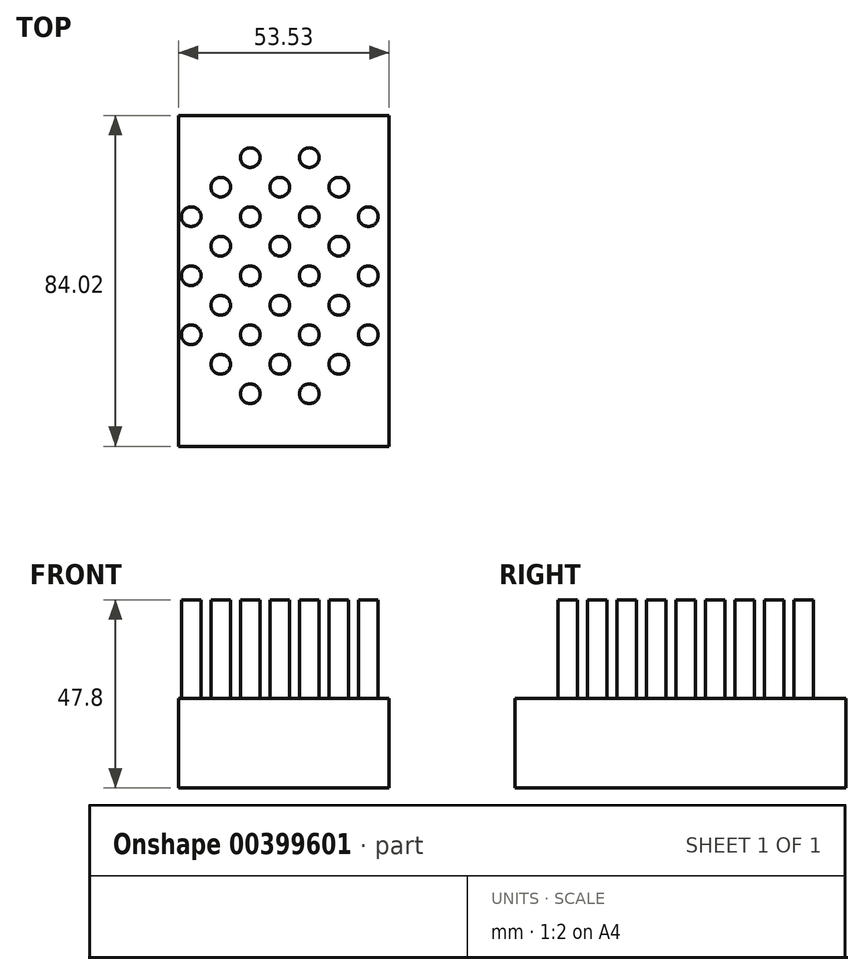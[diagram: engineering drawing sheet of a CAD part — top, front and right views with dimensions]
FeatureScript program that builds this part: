
annotation { "Feature Type Name" : "Feature", "Feature Type Description" : "" }
export const myFeature = defineFeature(function(context is Context, id is Id, definition is map)
    precondition{}
    {
        {
            var Q0;
            Q0=qCreatedBy(makeId("Top.planeOp"),FACE);
            var sketch = newSketch(context, id + "F0", { "sketchPlane" : qUnion([Q0])});
            skCircle(sketch, "E0", {"center": v(0, 8.36) * mm, "radius": 2.5 * mm});
            skCircle(sketch, "E1", {"center": v(7.5, 0.86) * mm, "radius": 2.5 * mm});
            skCircle(sketch, "E2.0.1.0", {"center": v(0, 23.36) * mm, "radius": 2.5 * mm});
            skCircle(sketch, "E2.0.1.1", {"center": v(7.5, 15.86) * mm, "radius": 2.5 * mm});
            skCircle(sketch, "E2.0.2.0", {"center": v(0, 38.36) * mm, "radius": 2.5 * mm});
            skCircle(sketch, "E2.0.2.1", {"center": v(7.5, 30.86) * mm, "radius": 2.5 * mm});
            skCircle(sketch, "E2.0.3.0", {"center": v(0, 53.36) * mm, "radius": 2.5 * mm});
            skCircle(sketch, "E2.0.3.1", {"center": v(7.5, 45.86) * mm, "radius": 2.5 * mm});
            skCircle(sketch, "E2.0.4.0", {"center": v(0, 68.36) * mm, "radius": 2.5 * mm});
            skCircle(sketch, "E2.0.4.1", {"center": v(7.5, 60.86) * mm, "radius": 2.5 * mm});
            skCircle(sketch, "E2.1.0.0", {"center": v(15, 8.36) * mm, "radius": 2.5 * mm});
            skCircle(sketch, "E2.1.0.1", {"center": v(22.5, 0.86) * mm, "radius": 2.5 * mm});
            skCircle(sketch, "E2.1.1.0", {"center": v(15, 23.36) * mm, "radius": 2.5 * mm});
            skCircle(sketch, "E2.1.1.1", {"center": v(22.5, 15.86) * mm, "radius": 2.5 * mm});
            skCircle(sketch, "E2.1.2.0", {"center": v(15, 38.36) * mm, "radius": 2.5 * mm});
            skCircle(sketch, "E2.1.2.1", {"center": v(22.5, 30.86) * mm, "radius": 2.5 * mm});
            skCircle(sketch, "E2.1.3.0", {"center": v(15, 53.36) * mm, "radius": 2.5 * mm});
            skCircle(sketch, "E2.1.3.1", {"center": v(22.5, 45.86) * mm, "radius": 2.5 * mm});
            skCircle(sketch, "E2.1.4.0", {"center": v(15, 68.36) * mm, "radius": 2.5 * mm});
            skCircle(sketch, "E2.1.4.1", {"center": v(22.5, 60.86) * mm, "radius": 2.5 * mm});
            skCircle(sketch, "E2.2.0.0", {"center": v(30, 8.36) * mm, "radius": 2.5 * mm});
            skCircle(sketch, "E2.2.0.1", {"center": v(37.5, 0.86) * mm, "radius": 2.5 * mm});
            skCircle(sketch, "E2.2.1.0", {"center": v(30, 23.36) * mm, "radius": 2.5 * mm});
            skCircle(sketch, "E2.2.1.1", {"center": v(37.5, 15.86) * mm, "radius": 2.5 * mm});
            skCircle(sketch, "E2.2.2.0", {"center": v(30, 38.36) * mm, "radius": 2.5 * mm});
            skCircle(sketch, "E2.2.2.1", {"center": v(37.5, 30.86) * mm, "radius": 2.5 * mm});
            skCircle(sketch, "E2.2.3.0", {"center": v(30, 53.36) * mm, "radius": 2.5 * mm});
            skCircle(sketch, "E2.2.3.1", {"center": v(37.5, 45.86) * mm, "radius": 2.5 * mm});
            skCircle(sketch, "E2.2.4.0", {"center": v(30, 68.36) * mm, "radius": 2.5 * mm});
            skCircle(sketch, "E2.2.4.1", {"center": v(37.5, 60.86) * mm, "radius": 2.5 * mm});
            skCircle(sketch, "E2.3.0.0", {"center": v(45, 8.36) * mm, "radius": 2.5 * mm});
            skCircle(sketch, "E2.3.0.1", {"center": v(52.5, 0.86) * mm, "radius": 2.5 * mm});
            skCircle(sketch, "E2.3.1.0", {"center": v(45, 23.36) * mm, "radius": 2.5 * mm});
            skCircle(sketch, "E2.3.1.1", {"center": v(52.5, 15.86) * mm, "radius": 2.5 * mm});
            skCircle(sketch, "E2.3.2.0", {"center": v(45, 38.36) * mm, "radius": 2.5 * mm});
            skCircle(sketch, "E2.3.2.1", {"center": v(52.5, 30.86) * mm, "radius": 2.5 * mm});
            skCircle(sketch, "E2.3.3.0", {"center": v(45, 53.36) * mm, "radius": 2.5 * mm});
            skCircle(sketch, "E2.3.3.1", {"center": v(52.5, 45.86) * mm, "radius": 2.5 * mm});
            skCircle(sketch, "E2.3.4.0", {"center": v(45, 68.36) * mm, "radius": 2.5 * mm});
            skCircle(sketch, "E2.3.4.1", {"center": v(52.5, 60.86) * mm, "radius": 2.5 * mm});
            skCircle(sketch, "E2.4.0.0", {"center": v(60, 8.36) * mm, "radius": 2.5 * mm});
            skCircle(sketch, "E2.4.0.1", {"center": v(67.5, 0.86) * mm, "radius": 2.5 * mm});
            skCircle(sketch, "E2.4.1.0", {"center": v(60, 23.36) * mm, "radius": 2.5 * mm});
            skCircle(sketch, "E2.4.1.1", {"center": v(67.5, 15.86) * mm, "radius": 2.5 * mm});
            skCircle(sketch, "E2.4.2.0", {"center": v(60, 38.36) * mm, "radius": 2.5 * mm});
            skCircle(sketch, "E2.4.2.1", {"center": v(67.5, 30.86) * mm, "radius": 2.5 * mm});
            skCircle(sketch, "E2.4.3.0", {"center": v(60, 53.36) * mm, "radius": 2.5 * mm});
            skCircle(sketch, "E2.4.3.1", {"center": v(67.5, 45.86) * mm, "radius": 2.5 * mm});
            skCircle(sketch, "E2.4.4.0", {"center": v(60, 68.36) * mm, "radius": 2.5 * mm});
            skCircle(sketch, "E2.4.4.1", {"center": v(67.5, 60.86) * mm, "radius": 2.5 * mm});
            skLineSegment(sketch, "E2.direction1", {"start": v(0, 8.36) * mm, "end": v(15, 8.36) * mm, "construction": true});
            skLineSegment(sketch, "E2.direction2", {"start": v(0, 8.36) * mm, "end": v(0, 23.36) * mm, "construction": true});
            skSolve(sketch);
        }
        {
            var Q0;
            Q0=makeQuery(id+"F0.imprint","IMPRINT",FACE,{"disambiguationData":[TD([[makeQuery(id+"F0.imprint","IMPRINT",EDGE,{"derivedFrom":sQuery(id+"F0.wireOp",EDGE,"E2.1.4.1")}),1.0]])]});
            var Q1;
            Q1=makeQuery(id+"F0.imprint","IMPRINT",FACE,{"disambiguationData":[TD([[makeQuery(id+"F0.imprint","IMPRINT",EDGE,{"derivedFrom":sQuery(id+"F0.wireOp",EDGE,"E2.2.3.0")}),1.0]])]});
            var Q2;
            Q2=makeQuery(id+"F0.imprint","IMPRINT",FACE,{"disambiguationData":[TD([[makeQuery(id+"F0.imprint","IMPRINT",EDGE,{"derivedFrom":sQuery(id+"F0.wireOp",EDGE,"E2.2.1.0")}),1.0]])]});
            var Q3;
            Q3=makeQuery(id+"F0.imprint","IMPRINT",FACE,{"disambiguationData":[TD([[makeQuery(id+"F0.imprint","IMPRINT",EDGE,{"derivedFrom":sQuery(id+"F0.wireOp",EDGE,"E2.2.0.0")}),1.0]])]});
            var Q4;
            Q4=makeQuery(id+"F0.imprint","IMPRINT",FACE,{"disambiguationData":[TD([[makeQuery(id+"F0.imprint","IMPRINT",EDGE,{"derivedFrom":sQuery(id+"F0.wireOp",EDGE,"E2.1.2.1")}),1.0]])]});
            var Q5;
            Q5=makeQuery(id+"F0.imprint","IMPRINT",FACE,{"disambiguationData":[TD([[makeQuery(id+"F0.imprint","IMPRINT",EDGE,{"derivedFrom":sQuery(id+"F0.wireOp",EDGE,"E2.2.4.1")}),1.0]])]});
            var Q6;
            Q6=makeQuery(id+"F0.imprint","IMPRINT",FACE,{"disambiguationData":[TD([[makeQuery(id+"F0.imprint","IMPRINT",EDGE,{"derivedFrom":sQuery(id+"F0.wireOp",EDGE,"E2.1.1.1")}),1.0]])]});
            var Q7;
            Q7=makeQuery(id+"F0.imprint","IMPRINT",FACE,{"disambiguationData":[TD([[makeQuery(id+"F0.imprint","IMPRINT",EDGE,{"derivedFrom":sQuery(id+"F0.wireOp",EDGE,"E2.1.0.1")}),1.0]])]});
            var Q8;
            Q8=makeQuery(id+"F0.imprint","IMPRINT",FACE,{"disambiguationData":[TD([[makeQuery(id+"F0.imprint","IMPRINT",EDGE,{"derivedFrom":sQuery(id+"F0.wireOp",EDGE,"E2.2.3.1")}),1.0]])]});
            var Q9;
            Q9=makeQuery(id+"F0.imprint","IMPRINT",FACE,{"disambiguationData":[TD([[makeQuery(id+"F0.imprint","IMPRINT",EDGE,{"derivedFrom":sQuery(id+"F0.wireOp",EDGE,"E2.2.1.1")}),1.0]])]});
            var Q10;
            Q10=makeQuery(id+"F0.imprint","IMPRINT",FACE,{"disambiguationData":[TD([[makeQuery(id+"F0.imprint","IMPRINT",EDGE,{"derivedFrom":sQuery(id+"F0.wireOp",EDGE,"E2.1.3.1")}),1.0]])]});
            var Q11;
            Q11=makeQuery(id+"F0.imprint","IMPRINT",FACE,{"disambiguationData":[TD([[makeQuery(id+"F0.imprint","IMPRINT",EDGE,{"derivedFrom":sQuery(id+"F0.wireOp",EDGE,"E2.2.2.0")}),1.0]])]});
            var Q12;
            Q12=makeQuery(id+"F0.imprint","IMPRINT",FACE,{"disambiguationData":[TD([[makeQuery(id+"F0.imprint","IMPRINT",EDGE,{"derivedFrom":sQuery(id+"F0.wireOp",EDGE,"E2.2.2.1")}),1.0]])]});
            var Q13;
            Q13=makeQuery(id+"F0.imprint","IMPRINT",FACE,{"disambiguationData":[TD([[makeQuery(id+"F0.imprint","IMPRINT",EDGE,{"derivedFrom":sQuery(id+"F0.wireOp",EDGE,"E2.3.3.0")}),1.0]])]});
            var Q14;
            Q14=makeQuery(id+"F0.imprint","IMPRINT",FACE,{"disambiguationData":[TD([[makeQuery(id+"F0.imprint","IMPRINT",EDGE,{"derivedFrom":sQuery(id+"F0.wireOp",EDGE,"E2.3.2.0")}),1.0]])]});
            var Q15;
            Q15=makeQuery(id+"F0.imprint","IMPRINT",FACE,{"disambiguationData":[TD([[makeQuery(id+"F0.imprint","IMPRINT",EDGE,{"derivedFrom":sQuery(id+"F0.wireOp",EDGE,"E2.3.1.0")}),1.0]])]});
            var Q16;
            Q16=makeQuery(id+"F0.imprint","IMPRINT",FACE,{"disambiguationData":[TD([[makeQuery(id+"F0.imprint","IMPRINT",EDGE,{"derivedFrom":sQuery(id+"F0.wireOp",EDGE,"E2.2.0.1")}),1.0]])]});
            var Q17;
            Q17=makeQuery(id+"F0.imprint","IMPRINT",FACE,{"disambiguationData":[TD([[makeQuery(id+"F0.imprint","IMPRINT",EDGE,{"derivedFrom":sQuery(id+"F0.wireOp",EDGE,"E2.3.0.0")}),1.0]])]});
            var Q18;
            Q18=makeQuery(id+"F0.imprint","IMPRINT",FACE,{"disambiguationData":[TD([[makeQuery(id+"F0.imprint","IMPRINT",EDGE,{"derivedFrom":sQuery(id+"F0.wireOp",EDGE,"E2.3.1.1")}),1.0]])]});
            var Q19;
            Q19=makeQuery(id+"F0.imprint","IMPRINT",FACE,{"disambiguationData":[TD([[makeQuery(id+"F0.imprint","IMPRINT",EDGE,{"derivedFrom":sQuery(id+"F0.wireOp",EDGE,"E2.3.2.1")}),1.0]])]});
            var Q20;
            Q20=makeQuery(id+"F0.imprint","IMPRINT",FACE,{"disambiguationData":[TD([[makeQuery(id+"F0.imprint","IMPRINT",EDGE,{"derivedFrom":sQuery(id+"F0.wireOp",EDGE,"E2.3.3.1")}),1.0]])]});
            var Q21;
            Q21=makeQuery(id+"F0.imprint","IMPRINT",FACE,{"disambiguationData":[TD([[makeQuery(id+"F0.imprint","IMPRINT",EDGE,{"derivedFrom":sQuery(id+"F0.wireOp",EDGE,"E2.1.3.0")}),1.0]])]});
            var Q22;
            Q22=makeQuery(id+"F0.imprint","IMPRINT",FACE,{"disambiguationData":[TD([[makeQuery(id+"F0.imprint","IMPRINT",EDGE,{"derivedFrom":sQuery(id+"F0.wireOp",EDGE,"E2.1.2.0")}),1.0]])]});
            var Q23;
            Q23=makeQuery(id+"F0.imprint","IMPRINT",FACE,{"disambiguationData":[TD([[makeQuery(id+"F0.imprint","IMPRINT",EDGE,{"derivedFrom":sQuery(id+"F0.wireOp",EDGE,"E2.1.1.0")}),1.0]])]});
            var Q24;
            Q24=makeQuery(id+"F0.imprint","IMPRINT",FACE,{"disambiguationData":[TD([[makeQuery(id+"F0.imprint","IMPRINT",EDGE,{"derivedFrom":sQuery(id+"F0.wireOp",EDGE,"E2.1.0.0")}),1.0]])]});
            var Q25;
            Q25=makeQuery(id+"F0.imprint","IMPRINT",FACE,{"disambiguationData":[TD([[makeQuery(id+"F0.imprint","IMPRINT",EDGE,{"derivedFrom":sQuery(id+"F0.wireOp",EDGE,"E2.0.1.1")}),1.0]])]});
            var Q26;
            Q26=makeQuery(id+"F0.imprint","IMPRINT",FACE,{"disambiguationData":[TD([[makeQuery(id+"F0.imprint","IMPRINT",EDGE,{"derivedFrom":sQuery(id+"F0.wireOp",EDGE,"E2.0.2.1")}),1.0]])]});
            var Q27;
            Q27=makeQuery(id+"F0.imprint","IMPRINT",FACE,{"disambiguationData":[TD([[makeQuery(id+"F0.imprint","IMPRINT",EDGE,{"derivedFrom":sQuery(id+"F0.wireOp",EDGE,"E2.0.3.1")}),1.0]])]});
            extrude(context, id + "F1", {"entities" : qUnion([Q0, Q1, Q2, Q3, Q4, Q5, Q6, Q7, Q8, Q9, Q10, Q11, Q12, Q13, Q14, Q15, Q16, Q17, Q18, Q19, Q20, Q21, Q22, Q23, Q24, Q25, Q26, Q27]), "depth" : 25 * mm});
        }
        {
            var Q0;
            Q0=qCreatedBy(makeId("Top.planeOp"),FACE);
            var sketch = newSketch(context, id + "F2", { "sketchPlane" : qUnion([Q0])});
            skLineSegment(sketch, "E3.bottom", {"start": v(4.25, 71.54) * mm, "end": v(57.78, 71.54) * mm});
            skLineSegment(sketch, "E3.top", {"start": v(4.25, -12.48) * mm, "end": v(57.78, -12.48) * mm});
            skLineSegment(sketch, "E3.left", {"start": v(4.25, 71.54) * mm, "end": v(4.25, -12.48) * mm});
            skLineSegment(sketch, "E3.right", {"start": v(57.78, 71.54) * mm, "end": v(57.78, -12.48) * mm});
            skSolve(sketch);
        }
        {
            var Q0;
            Q0=makeQuery(id+"F2.imprint","IMPRINT",FACE,{"disambiguationData":[TD([[makeQuery(id+"F2.imprint","IMPRINT",EDGE,{"derivedFrom":sQuery(id+"F2.wireOp",EDGE,"E3.bottom")}),-1.0]])]});
            extrude(context, id + "F3", {"entities" : qUnion([Q0]), "operationType" : NewBodyOperationType.ADD, "oppositeDirection" : true, "depth" : 22.8 * mm});
        }
    });
